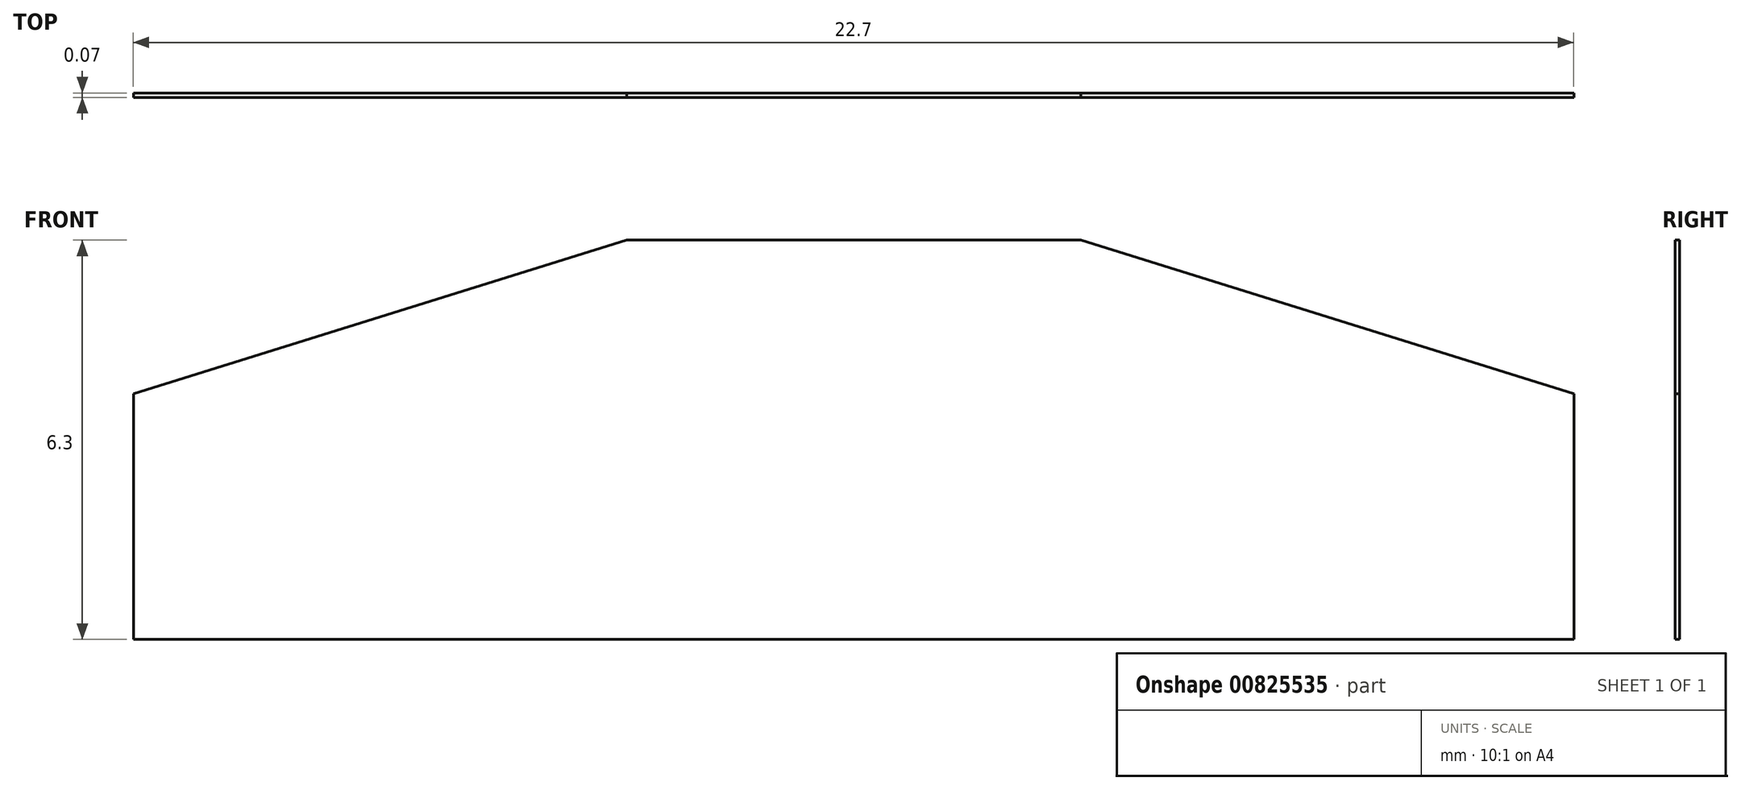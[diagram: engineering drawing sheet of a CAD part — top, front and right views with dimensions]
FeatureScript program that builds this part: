
annotation { "Feature Type Name" : "Feature", "Feature Type Description" : "" }
export const myFeature = defineFeature(function(context is Context, id is Id, definition is map)
    precondition{}
    {
        {
            var Q0;
            Q0=qCreatedBy(makeId("Front.planeOp"),FACE);
            var sketch = newSketch(context, id + "F0", { "sketchPlane" : qUnion([Q0])});
            skLineSegment(sketch, "E0.bottom", {"start": v(-4.59, 2.55) * mm, "end": v(18.11, 2.55) * mm});
            skLineSegment(sketch, "E0.top", {"start": v(-4.59, -3.75) * mm, "end": v(18.11, -3.75) * mm});
            skLineSegment(sketch, "E0.left", {"start": v(-4.59, 2.55) * mm, "end": v(-4.59, -3.75) * mm});
            skLineSegment(sketch, "E0.right", {"start": v(18.11, 2.55) * mm, "end": v(18.11, -3.75) * mm});
            skSolve(sketch);
        }
        {
            var Q0;
            Q0 = qSketchRegion(id + "F0", true);
            extrude(context, id + "F1", {"entities" : qUnion([Q0]), "depth" : 0.07 * mm, "offsetDistance" : 25 * mm});
        }
        {
            var Q0;
            Q0=makeQuery(id+"F1.opExtrude","CAP_FACE",FACE,{"disambiguationData":[OSD([sQuery(id+"F0.wireOp",EDGE,"E0.bottom"),sQuery(id+"F0.wireOp",EDGE,"E0.top"),sQuery(id+"F0.wireOp",EDGE,"E0.left"),sQuery(id+"F0.wireOp",EDGE,"E0.right")])],"isStart":false});
            var sketch = newSketch(context, id + "F2", { "sketchPlane" : qUnion([Q0])});
            skLineSegment(sketch, "E1", {"start": v(-4.59, 0.12) * mm, "end": v(3.19, 2.55) * mm});
            skLineSegment(sketch, "E2", {"start": v(3.19, 2.55) * mm, "end": v(-4.59, 2.55) * mm});
            skLineSegment(sketch, "E3", {"start": v(-4.59, 2.55) * mm, "end": v(-4.59, 0.12) * mm});
            skLineSegment(sketch, "E4", {"start": v(10.34, 2.55) * mm, "end": v(18.11, 0.12) * mm});
            skLineSegment(sketch, "E5", {"start": v(18.11, 0.12) * mm, "end": v(18.11, 2.55) * mm});
            skLineSegment(sketch, "E6", {"start": v(18.11, 2.55) * mm, "end": v(10.34, 2.55) * mm});
            skSolve(sketch);
        }
        {
            var Q0;
            Q0 = qSketchRegion(id + "F2", true);
            extrude(context, id + "F3", {"entities" : qUnion([Q0]), "operationType" : NewBodyOperationType.REMOVE, "oppositeDirection" : true, "depth" : 25 * mm, "offsetDistance" : 25 * mm});
        }
    });
